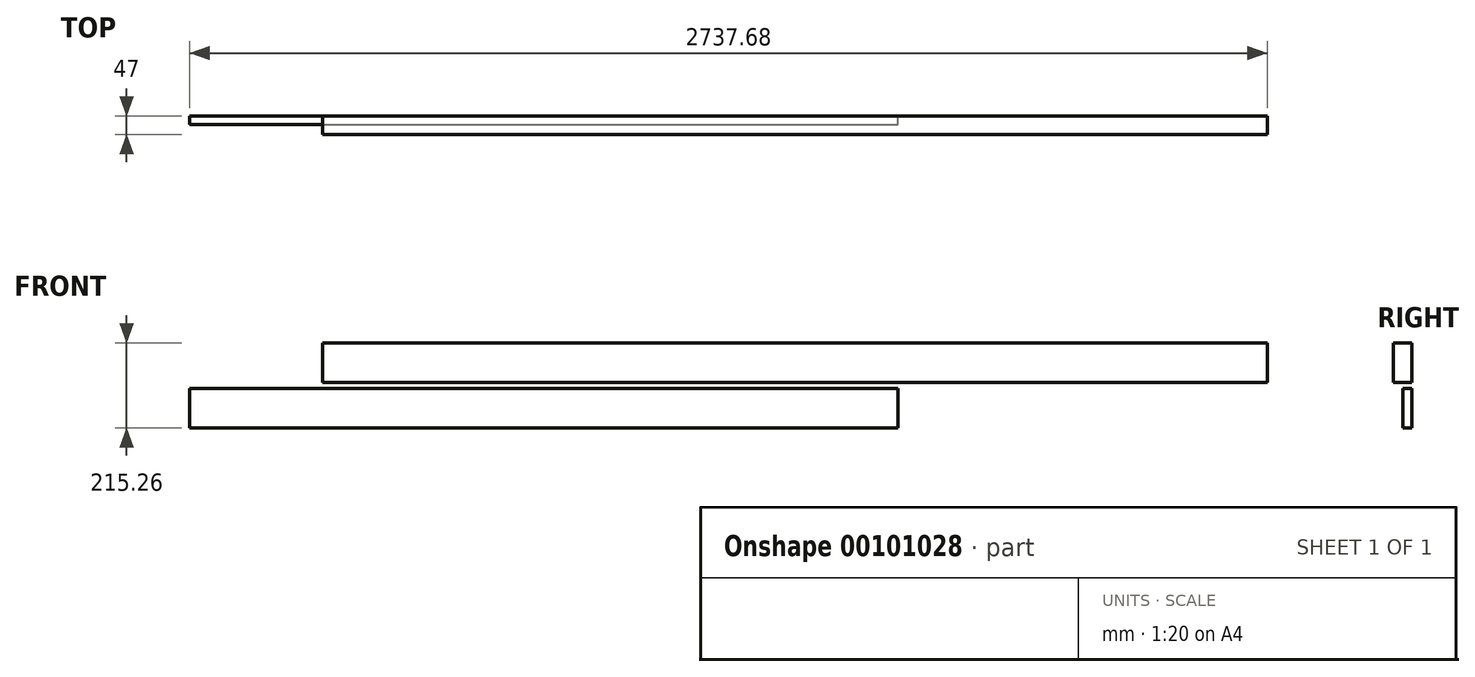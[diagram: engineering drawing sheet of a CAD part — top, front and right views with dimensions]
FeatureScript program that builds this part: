
annotation { "Feature Type Name" : "Feature", "Feature Type Description" : "" }
export const myFeature = defineFeature(function(context is Context, id is Id, definition is map)
    precondition{}
    {
        {
            var Q0;
            Q0=qCreatedBy(makeId("Front.planeOp"),FACE);
            var sketch = newSketch(context, id + "F0", { "sketchPlane" : qUnion([Q0])});
            skLineSegment(sketch, "E0.bottom", {"start": v(-1299.57, 75.05) * mm, "end": v(1100.43, 75.05) * mm});
            skLineSegment(sketch, "E0.top", {"start": v(-1299.57, -24.95) * mm, "end": v(1100.43, -24.95) * mm});
            skLineSegment(sketch, "E0.left", {"start": v(-1299.57, 75.05) * mm, "end": v(-1299.57, -24.95) * mm});
            skLineSegment(sketch, "E0.right", {"start": v(1100.43, 75.05) * mm, "end": v(1100.43, -24.95) * mm});
            skSolve(sketch);
        }
        {
            var Q0;
            Q0=makeQuery(id+"F0.imprint","IMPRINT",FACE,{"disambiguationData":[TD([[makeQuery(id+"F0.imprint","IMPRINT",EDGE,{"derivedFrom":sQuery(id+"F0.wireOp",EDGE,"E0.bottom")}),-1.0]])]});
            extrude(context, id + "F1", {"entities" : qUnion([Q0]), "depth" : 47 * mm});
        }
        {
            var Q0;
            Q0=qCreatedBy(makeId("Front.planeOp"),FACE);
            var sketch = newSketch(context, id + "F2", { "sketchPlane" : qUnion([Q0])});
            skLineSegment(sketch, "E1.bottom", {"start": v(-1637.25, -40.2) * mm, "end": v(162.75, -40.2) * mm});
            skLineSegment(sketch, "E1.top", {"start": v(-1637.25, -140.2) * mm, "end": v(162.75, -140.2) * mm});
            skLineSegment(sketch, "E1.left", {"start": v(-1637.25, -40.2) * mm, "end": v(-1637.25, -140.2) * mm});
            skLineSegment(sketch, "E1.right", {"start": v(162.75, -40.2) * mm, "end": v(162.75, -140.2) * mm});
            skSolve(sketch);
        }
        {
            var Q0;
            Q0 = qSketchRegion(id + "F2", true);
            extrude(context, id + "F3", {"entities" : qUnion([Q0]), "depth" : 22 * mm});
        }
    });
